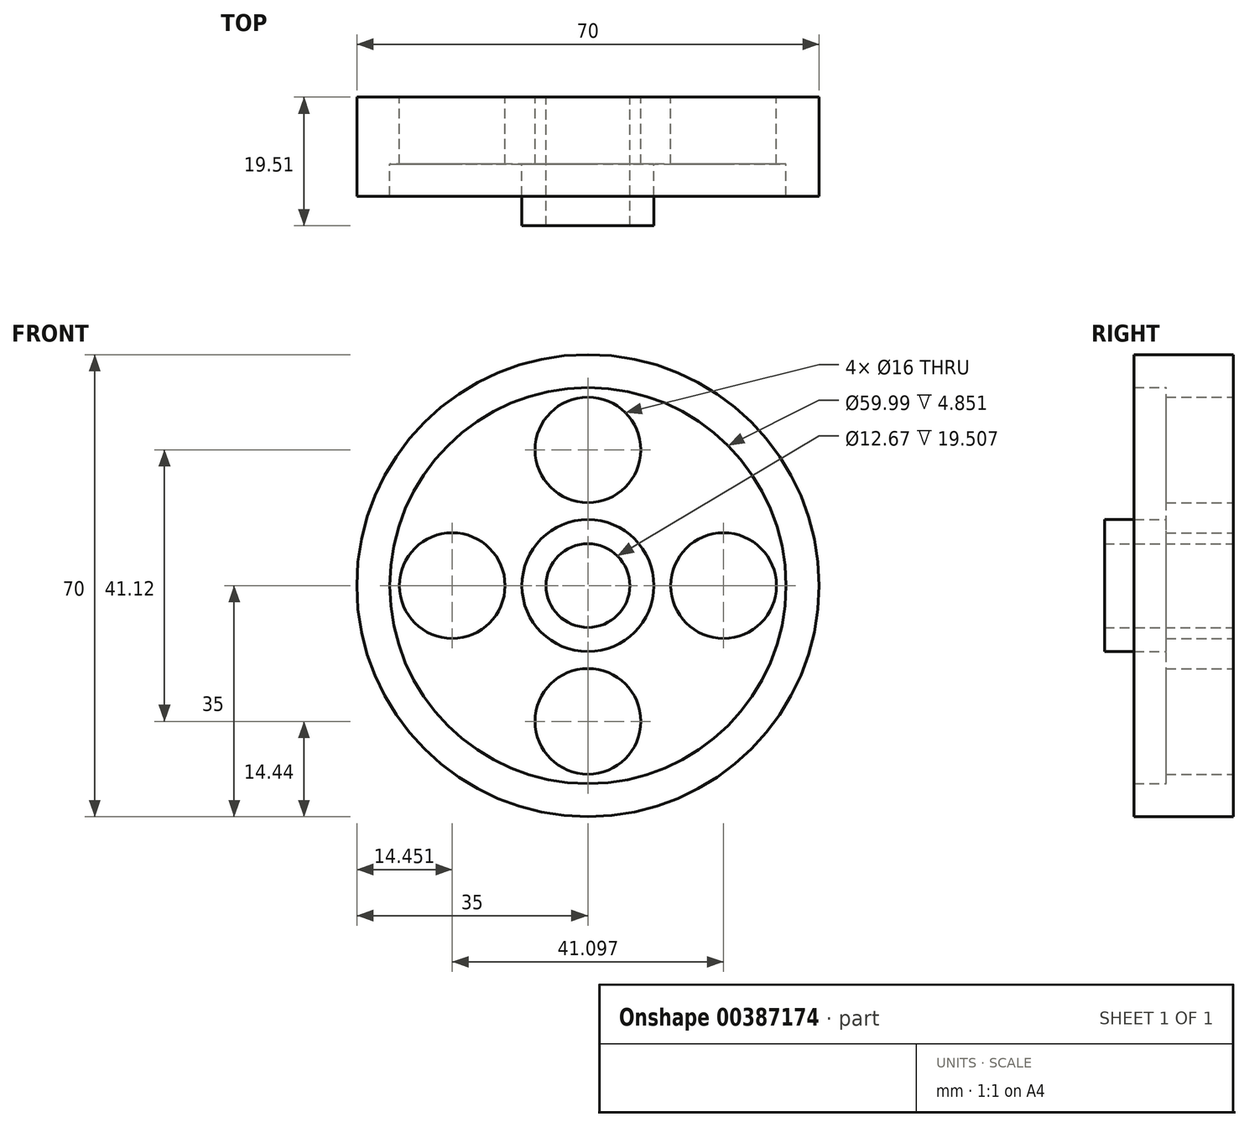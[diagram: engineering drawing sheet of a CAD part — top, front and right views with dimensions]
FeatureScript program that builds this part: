
annotation { "Feature Type Name" : "Feature", "Feature Type Description" : "" }
export const myFeature = defineFeature(function(context is Context, id is Id, definition is map)
    precondition{}
    {
        {
            var Q0;
            Q0=qCreatedBy(makeId("Front.planeOp"),FACE);
            var sketch = newSketch(context, id + "F0", { "sketchPlane" : qUnion([Q0])});
            skCircle(sketch, "E0", {"center": v(0, 0) * mm, "radius": 35 * mm});
            skCircle(sketch, "E1", {"center": v(0, 0) * mm, "radius": 30 * mm});
            skCircle(sketch, "E2", {"center": v(0, 0) * mm, "radius": 6.34 * mm});
            skCircle(sketch, "E3", {"center": v(0, 0) * mm, "radius": 10 * mm});
            skLineSegment(sketch, "E4", {"start": v(0, 0) * mm, "end": v(0, 12.56) * mm});
            skCircle(sketch, "E5", {"center": v(0, 20.56) * mm, "radius": 8 * mm});
            skLineSegment(sketch, "E6.MirrorCS", {"start": v(0, 0) * mm, "end": v(0, -12.56) * mm});
            skCircle(sketch, "E7.MirrorC", {"center": v(0, -20.56) * mm, "radius": 8 * mm});
            skLineSegment(sketch, "E8", {"start": v(0, 0) * mm, "end": v(12.55, 0) * mm});
            skCircle(sketch, "E9", {"center": v(20.55, 0) * mm, "radius": 8 * mm});
            skCircle(sketch, "E10.MirrorC", {"center": v(-20.55, 0) * mm, "radius": 8 * mm});
            skSolve(sketch);
        }
        {
            var Q0;
            Q0=makeQuery(id+"F0.imprint","IMPRINT",FACE,{"disambiguationData":[TD([[makeQuery(id+"F0.imprint","IMPRINT",EDGE,{"derivedFrom":sQuery(id+"F0.wireOp",EDGE,"E1")}),1.0]])]});
            extrude(context, id + "F1", {"entities" : qUnion([Q0]), "depth" : 10.16 * mm});
        }
        {
            var Q0;
            Q0=makeQuery(id+"F0.imprint","IMPRINT",FACE,{"disambiguationData":[TD([[makeQuery(id+"F0.imprint","IMPRINT",EDGE,{"derivedFrom":sQuery(id+"F0.wireOp",EDGE,"E0")}),1.0]])]});
            extrude(context, id + "F2", {"entities" : qUnion([Q0]), "operationType" : NewBodyOperationType.ADD, "depth" : 15 * mm});
        }
        {
            var Q0;
            {var subQ0=sQuery(id+"F0.wireOp",EDGE,"E8");var subQ1=sQuery(id+"F0.wireOp",EDGE,"E2");var subQ2=makeQuery(id+"F0.imprint","INTERSECT",VERTEX,{"derivedFrom":[subQ1,subQ0]});Q0=makeQuery(id+"F0.imprint","IMPRINT",FACE,{"disambiguationData":[TD([[makeQuery(id+"F0.imprint","IMPRINT",EDGE,{"disambiguationData":[TD([[subQ2,1.0]])],"derivedFrom":subQ1}),-1.0]])]});}
            var Q1;
            {var subQ0=sQuery(id+"F0.wireOp",EDGE,"E4");var subQ1=sQuery(id+"F0.wireOp",EDGE,"E2");var subQ2=makeQuery(id+"F0.imprint","INTERSECT",VERTEX,{"derivedFrom":[subQ1,subQ0]});Q1=makeQuery(id+"F0.imprint","IMPRINT",FACE,{"disambiguationData":[TD([[makeQuery(id+"F0.imprint","IMPRINT",EDGE,{"disambiguationData":[TD([[subQ2,1.0]])],"derivedFrom":subQ1}),-1.0]])]});}
            var Q2;
            {var subQ0=sQuery(id+"F0.wireOp",EDGE,"E4");var subQ1=sQuery(id+"F0.wireOp",EDGE,"E2");var subQ2=makeQuery(id+"F0.imprint","INTERSECT",VERTEX,{"derivedFrom":[subQ1,subQ0]});Q2=makeQuery(id+"F0.imprint","IMPRINT",FACE,{"disambiguationData":[TD([[makeQuery(id+"F0.imprint","IMPRINT",EDGE,{"disambiguationData":[TD([[subQ2,-1.0]])],"derivedFrom":subQ1}),-1.0]])]});}
            extrude(context, id + "F3", {"entities" : qUnion([Q0, Q1, Q2]), "operationType" : NewBodyOperationType.ADD, "depth" : 19.5 * mm});
        }
    });
